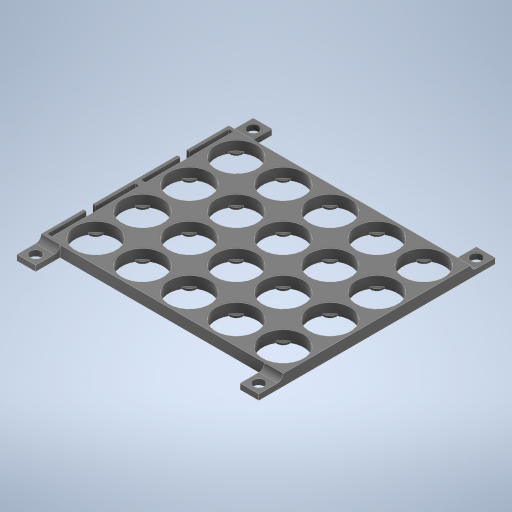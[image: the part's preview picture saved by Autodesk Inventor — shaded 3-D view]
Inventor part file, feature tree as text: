
AUTODESK INVENTOR PART (.ipt)
format: ipt  version: 2024.2 (Build 282272000, 272)  size: 577,024 bytes
history: native  units: in
note: dims shown in document units (in); Inventor stores cm internally (conversion verified against a paired STEP export)
features: sketch x4, extrude x4, pattern_linear x2, fillet x1, hole x1
ambient origin geometry x8: Origin, YZ Plane, XZ Plane, XY Plane, X Axis, Y Axis, Z Axis, Center Point
bodies: Body1 (feature_tree)
feature tree (12):
  sketch  "Sketch1"  dims[d18=0.0in d20=0.0in]
  extrude  "thickness"  TaperAngle=0.0deg  [1 undecoded]
  extrude  "catcher"  Depth=0.2756in
  pattern_linear  "gridPattern"  Count1=5 Spacing1=0.9843in
  extrude  "Extrusion5"  Depth=0.9843in
  extrude  "Extrusion9"  Depth=0.9843in
  fillet  "Fillet3"  Radius=0.1969in
  hole  "Hole4"  [1 undecoded]
  pattern_linear  "Rectangular Pattern4"  Spacing1=0.0in  [1 undecoded]
  sketch  "Sketch2"  dims[d27=0.2756in d28=0.2756in]
  sketch  "Sketch14"  dims[d29=0.2756in d30=1.9685in d32=0.9843in]
  sketch  "Sketch15"  dims[d33=1.5748in d35=0.9843in d36=0.9843in d37=0.9843in d41=0.1969in d46=0.2362in d47=0.0in d48=0.0591in d49=0.0591in d99=0.3937in d100=0.5118in d103=0.1181in d104=0.0in d105=0.1181in d106=0.2362in d107=0.12in d108=0.375in d109=0.25in d110=0.5635in d111=1.0in d112=0.0in d119=0.7874in d121=4.6853in d122=0.7874in d124=4.5673in d17=0.5in d19=0.5in d21=0.5in d22=0.0344in d31=0.0344in d38=0.5in d39=0.0344in d40=0.5in d57=0.5in d58=0.0344in d59=0.5in d60=0.0344in d66=1.0in d67=1.0in d68=1.0in d69=0.15in d70=0.25in d71=0.375in d72=0.5635in d73=0.75in d74=0.8108in d75=0.0625in d76=0.75in d77=0.375in d120=0.0344in d123=0.25in d125=0.5635in d126=0.75in d127=0.8108in d128=0.0625in d129=0.75in d130=0.375in]
note: 3 required parameter values undecoded (feature->parameter linkage not recoverable at this tier; creation-order binding heuristic only, values carry confidence <= 0.55)
